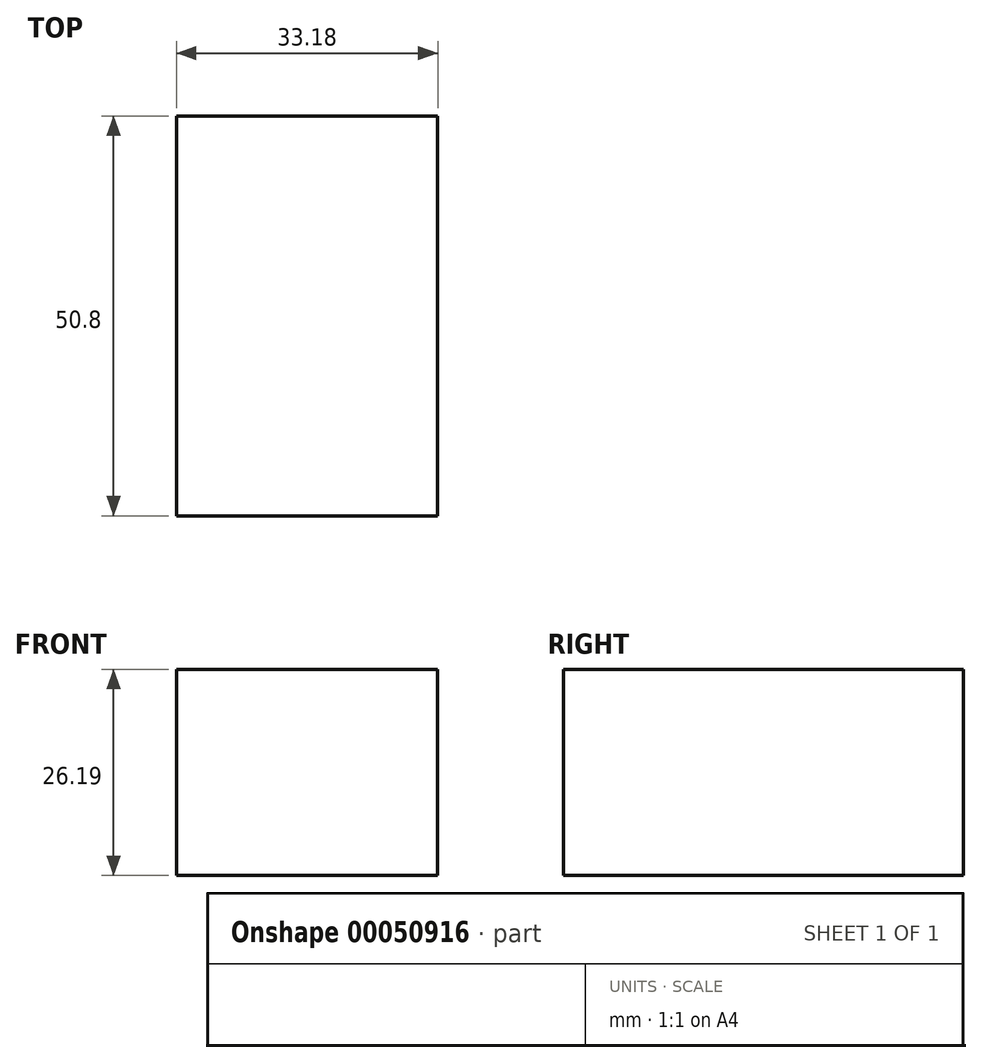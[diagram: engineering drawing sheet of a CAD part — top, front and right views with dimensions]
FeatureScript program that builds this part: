
annotation { "Feature Type Name" : "Feature", "Feature Type Description" : "" }
export const myFeature = defineFeature(function(context is Context, id is Id, definition is map)
    precondition{}
    {
        {
            var Q0;
            Q0=qCreatedBy(makeId("Front.planeOp"),FACE);
            var sketch = newSketch(context, id + "F0", { "sketchPlane" : qUnion([Q0])});
            skLineSegment(sketch, "E0.bottom", {"start": v(-56.33, 35.06) * mm, "end": v(-23.15, 35.06) * mm});
            skLineSegment(sketch, "E0.top", {"start": v(-56.33, 8.87) * mm, "end": v(-23.15, 8.87) * mm});
            skLineSegment(sketch, "E0.left", {"start": v(-56.33, 35.06) * mm, "end": v(-56.33, 8.87) * mm});
            skLineSegment(sketch, "E0.right", {"start": v(-23.15, 35.06) * mm, "end": v(-23.15, 8.87) * mm});
            skSolve(sketch);
        }
        {
            var Q0;
            Q0 = qSketchRegion(id + "F0", true);
            extrude(context, id + "F1", {"entities" : qUnion([Q0]), "depth" : 50.8 * mm});
        }
    });
